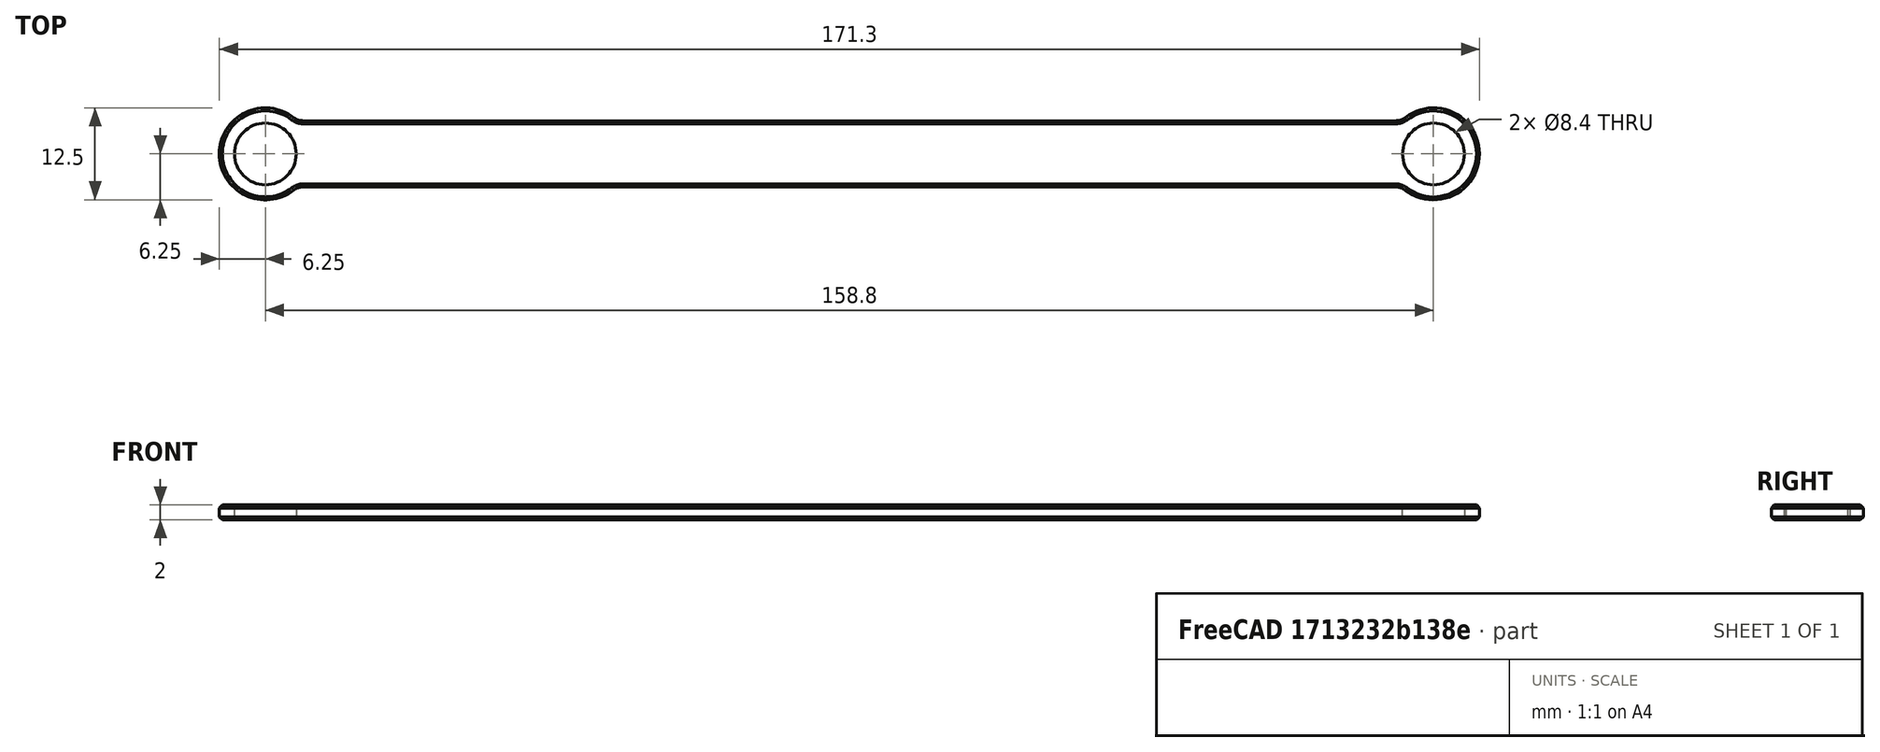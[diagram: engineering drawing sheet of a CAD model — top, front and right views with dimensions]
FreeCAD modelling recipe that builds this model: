
FCSTD DOCUMENT  (FreeCAD 0.18R16146 (Git))
Label: ResizedLeftChainSecondAuxiliaryRod
License: All rights reserved
LicenseURL: http://en.wikipedia.org/wiki/All_rights_reserved
objects: Part::Feature×1, PartDesign::FeatureBase×1, Sketcher::SketchObject×1, PartDesign::Pocket×1, PartDesign::Body×1
note: 6 computed .brp shape members not serialized (recipe doc carries the construction recipe); baked Part::Feature solids carry a one-line shape summary decoded from their .brp

FEATURE [Part::Feature] Part__Feature008  label="LeftChainSecondAuxiliaryRod"
  Placement = pos=(10.2057,271.336,-104.204) rot=(-0.180229,0.983625,0;3.14159rad)
  shape: bbox 161 x 68.8 x 2 mm, 33 faces (baked)
FEATURE [PartDesign::FeatureBase] BaseFeature
  BaseFeature = -> Part__Feature008
FEATURE [Sketcher::SketchObject] Sketch
  ExternalGeometry = -> [BaseFeature]
  MapMode = 5
  Placement = pos=(0,0,1) rot=(0,0,1;0rad)
  Support = -> [BaseFeature]
  sketch-geometry (2):
    g0: Circle CenterX=-79.4 CenterY=0 CenterZ=0 NormalX=0 NormalY=0 NormalZ=1 AngleXU=0 Radius=4.2
    g1: Circle CenterX=79.4 CenterY=0 CenterZ=0 NormalX=0 NormalY=0 NormalZ=1 AngleXU=0 Radius=4.2
  constraints (4):
    c: Coincident(g0,g-4)
    c: Coincident(g1,g-6)
    c: Radius(g1) = 4.2
    c: Radius(g0) = 4.2
FEATURE [PartDesign::Pocket] Pocket
  BaseFeature = -> BaseFeature
  Length = 5
  Length2 = 100
  Profile = -> Sketch
  Type = 1
FEATURE [PartDesign::Body] Body  label="LeftChainSecondAuxiliaryRod001"
  BaseFeature = -> Part__Feature008
  Group = -> [BaseFeature,Sketch,Pocket]
  Origin = -> Origin
  Tip = -> Pocket
